# Revit family: Electronics_Communication_Talkaphone_Fixed-5-Station-Analog-AOR-Command-Unit
name_source: partatom
category: Telephone Devices
units: mm (PartAtom-declared; Revit-internal decimal feet)

## family parameters
Cut with Voids When Loaded = No
Host = Face
Maintain Annotation Orientation = No
OmniClass Number = 23.37.27.17
Part Type = Normal
Room Calculation Point = No
Round Connector Dimension = Use Diameter
Shared = No

## types (1)
- Fixed 5-Station Analog Command Unit
    Apparent Load = 0 VA
    Assembly Code = D5030300
    Call Station Options = Indoor Flush Mount Model: AOR-CSE-FM, Indoor Surface Mount Model: AOR-CSE-SM
    Communication = Built-in handset with volume control receives calls—selectively originate calls using the front panel interface buttons
    Connection = Internal terminal block
    Connectivity = Supports one (1) analog phone line (PSTN line) for off-site dialing
    Construction = Stainless steel faceplate with 16 gauge, powder coated steel enclosure
    Default Elevation = 48.00"
    Depth = 4.12"
    Description = THIS FULLY INTEGRATED FIXED STATION ANALOG COMMAND UNIT ACCOMMODATES UP TO 5 ADA-COMPLIANT AREA OF RESCUE STATIONS. THE UNIT PROVIDES BOTH AUDIBLE AND VISUAL INDICATORS FOR AN INCOMING CALL—LED LIGHTS INDICATE THE CALLING LOCATION.
    Edition number = 1
    Environment = For indoor use
    Fault Monitoring = Activation of any AOR Station, opens/shorts on AOR Station cabling, PSTN line connection, 24VDC input power failure, low battery backup (low voltage detected), and system ground fault
    Fault Reset = Keyed switch provided for authorized personnel to temporarily silence while faults are corrected or to re-test/reset fault indicators after faults have been resolved
    Height = 18.00"
    Keynote = 27 30 00
    Manufacturer = Talkaphone
    Model = AOR-5
    Mounting = Flush mount with optional trim ring or surface mount
    Number of Poles = 1
    Power Factor = 1
    Power Source = 24VDC, 2A (includes built-in 24-hour battery backup)
    Product Guid = ecdf64c1-b427-4f7f-b5bc-35d875522d34
    Product Material = Talkaphone - Stainless Steel and White Painted Steel
    Product data url = https://www.bimobject.com
    Programming = Programming of the Analog Command Unit and Analog Stations can be carried out via touch-tone commands sent through a Sub-Command Unit or a remote PSTN phone call. All programming is stored on non-volatile EEPROMs.
    Supervision Relay = Activation of any AOR Station, opens/shorts on AOR Station cabling, 24VDC input power failure, low battery backup (low voltage detected), and system ground fault
    URL = https://www.talkaphone.com
    Voltage = 24 V
    Warranty = 5-year limited warranty
    Width = 13.25"
    Wiring = One (1) twisted, shielded 18-24 AWG pair per station

## geometry (parser evidence)
native form markers: Sweep x2
no freeform markers — native parametric forms only
